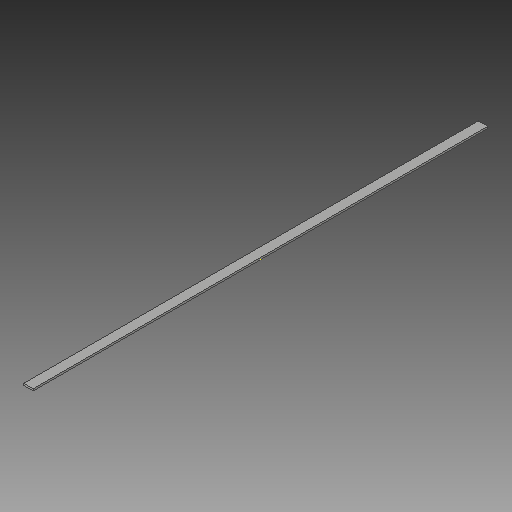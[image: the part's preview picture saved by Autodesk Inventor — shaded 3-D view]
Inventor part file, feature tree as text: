
AUTODESK INVENTOR PART (.ipt)
format: ipt  version: 2018 (Build 220112000, 112)  size: 94,720 bytes
history: native  units: mm
features: extrude x1, other x1, sketch x1
ambient origin geometry x8: Origin, YZ Plane, XZ Plane, XY Plane, X Axis, Y Axis, Z Axis, Center Point
bodies: Solid1 (feature_tree)
feature tree (3):
  extrude  "Extrusion1"  Depth=5.0mm
  other  "Work Axis1"
  sketch  "Sketch1"  dims[d0=25.0mm d1=5.0mm d2=1208.95mm d3=0.0mm]
